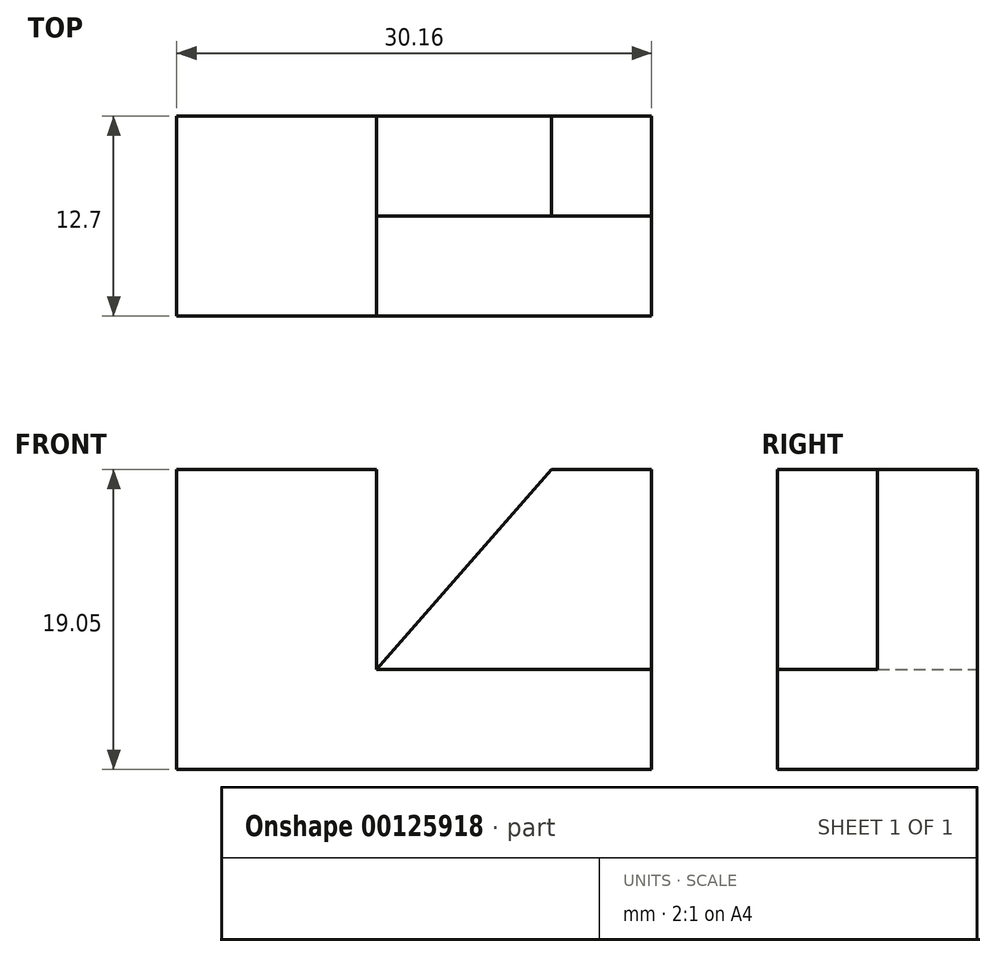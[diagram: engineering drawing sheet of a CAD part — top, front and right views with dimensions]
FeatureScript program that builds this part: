
annotation { "Feature Type Name" : "Feature", "Feature Type Description" : "" }
export const myFeature = defineFeature(function(context is Context, id is Id, definition is map)
    precondition{}
    {
        {
            var Q0;
            Q0=qCreatedBy(makeId("Front.planeOp"),FACE);
            var sketch = newSketch(context, id + "F0", { "sketchPlane" : qUnion([Q0])});
            skLineSegment(sketch, "E0.bottom", {"start": v(-25.16, 22.87) * mm, "end": v(5, 22.87) * mm});
            skLineSegment(sketch, "E0.top", {"start": v(-25.16, 16.52) * mm, "end": v(5, 16.52) * mm});
            skLineSegment(sketch, "E0.left", {"start": v(-25.16, 22.87) * mm, "end": v(-25.16, 16.52) * mm});
            skLineSegment(sketch, "E0.right", {"start": v(5, 22.87) * mm, "end": v(5, 16.52) * mm});
            skLineSegment(sketch, "E1.bottom", {"start": v(-25.16, 22.87) * mm, "end": v(-12.46, 22.87) * mm});
            skLineSegment(sketch, "E1.top", {"start": v(-25.16, 35.57) * mm, "end": v(-12.46, 35.57) * mm});
            skLineSegment(sketch, "E1.left", {"start": v(-25.16, 22.87) * mm, "end": v(-25.16, 35.57) * mm});
            skLineSegment(sketch, "E1.right", {"start": v(-12.46, 22.87) * mm, "end": v(-12.46, 35.57) * mm});
            skSolve(sketch);
        }
        {
            var Q0;
            Q0 = qSketchRegion(id + "F0", true);
            extrude(context, id + "F1", {"entities" : qUnion([Q0]), "depth" : 12.7 * mm, "offsetDistance" : 25.4 * mm});
        }
        {
            var Q0;
            Q0=makeQuery(id+"F1.opExtrude","SWEPT_FACE",FACE,{"disambiguationData":[OSD([sQuery(id+"F0.wireOp",EDGE,"E0.bottom")])]});
            var sketch = newSketch(context, id + "F2", { "sketchPlane" : qUnion([Q0])});
            skLineSegment(sketch, "E2.bottom", {"start": v(5, 0) * mm, "end": v(-1.35, 0) * mm});
            skLineSegment(sketch, "E2.top", {"start": v(5, -6.35) * mm, "end": v(-1.35, -6.35) * mm});
            skLineSegment(sketch, "E2.left", {"start": v(5, 0) * mm, "end": v(5, -6.35) * mm});
            skLineSegment(sketch, "E2.right", {"start": v(-1.35, 0) * mm, "end": v(-1.35, -6.35) * mm});
            skSolve(sketch);
        }
        {
            var Q0;
            Q0 = qSketchRegion(id + "F2", true);
            extrude(context, id + "F3", {"entities" : qUnion([Q0]), "operationType" : NewBodyOperationType.ADD, "depth" : 12.7 * mm, "offsetDistance" : 25.4 * mm});
        }
        {
            var Q0;
            Q0=makeQuery(id+"F3.boolean.opBoolean","MERGE",FACE,{"derivedFrom":[makeQuery(id+"F1.opExtrude","CAP_FACE",FACE,{"disambiguationData":[OSD([sQuery(id+"F0.wireOp",EDGE,"E0.bottom"),sQuery(id+"F0.wireOp",EDGE,"E0.top"),sQuery(id+"F0.wireOp",EDGE,"E0.left"),sQuery(id+"F0.wireOp",EDGE,"E0.right"),sQuery(id+"F0.wireOp",EDGE,"E1.top"),sQuery(id+"F0.wireOp",EDGE,"E1.left"),sQuery(id+"F0.wireOp",EDGE,"E1.right")])],"isStart":true}),makeQuery(id+"F3.opExtrude","SWEPT_FACE",FACE,{"disambiguationData":[OSD([sQuery(id+"F2.wireOp",EDGE,"E2.bottom")])]})]});
            var sketch = newSketch(context, id + "F4", { "sketchPlane" : qUnion([Q0])});
            skLineSegment(sketch, "E3", {"start": v(1.35, 35.57) * mm, "end": v(12.46, 22.87) * mm});
            skSolve(sketch);
        }
        {
            var Q0;
            Q0 = qSketchRegion(id + "F4", true);
            var Q1;
            Q1=makeQuery(id+"F4.imprint","IMPRINT",FACE,{"disambiguationData":[TD([[makeQuery(id+"F4.imprint","IMPRINT",EDGE,{"derivedFrom":sQuery(id+"F4.wireOp",EDGE,"E3")}),-1.0]])]});
            extrude(context, id + "F5", {"entities" : qUnion([Q0, Q1]), "operationType" : NewBodyOperationType.ADD, "oppositeDirection" : true, "depth" : 6.35 * mm, "offsetDistance" : 25.4 * mm});
        }
    });
